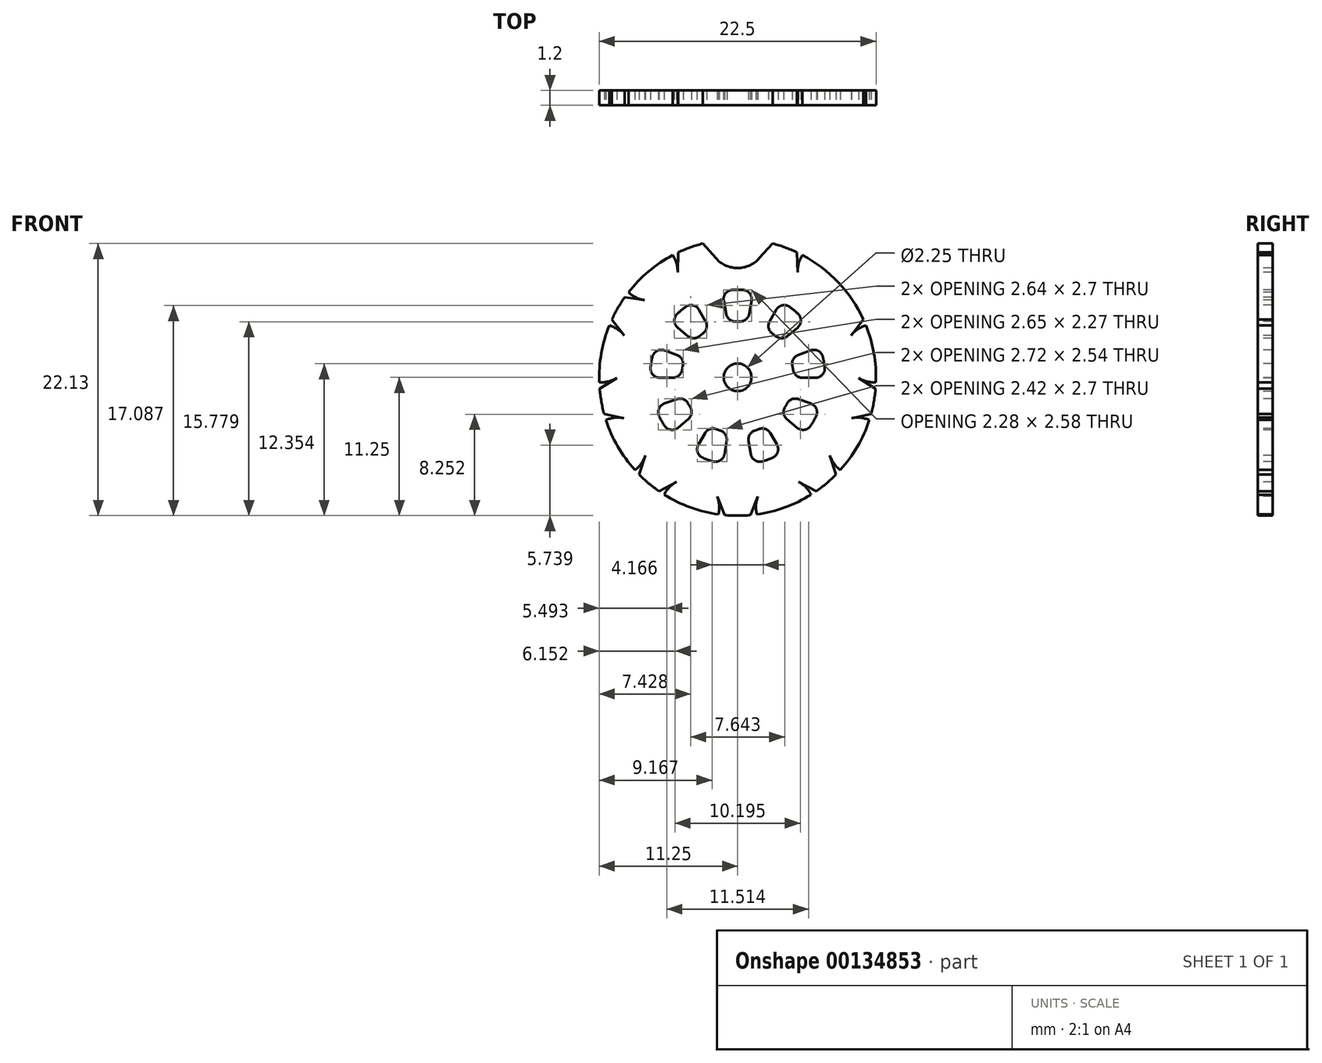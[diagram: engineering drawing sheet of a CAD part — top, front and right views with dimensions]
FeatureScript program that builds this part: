
annotation { "Feature Type Name" : "Feature", "Feature Type Description" : "" }
export const myFeature = defineFeature(function(context is Context, id is Id, definition is map)
    precondition{}
    {
        {
            var Q0;
            Q0=qCreatedBy(makeId("Front.planeOp"),FACE);
            var sketch = newSketch(context, id + "F0", { "sketchPlane" : qUnion([Q0])});
            skCircle(sketch, "E0", {"center": v(0, 0) * mm, "radius": 7.5 * mm});
            skSolve(sketch);
        }
        {
            var Q0;
            Q0=qSketchRegion(id+"F0",true);
            extrude(context, id + "F1", {"entities" : qUnion([Q0]), "depth" : 0.8 * mm});
        }
        {
            var Q0;
            Q0=makeQuery(id+"F1.opExtrude","CAP_FACE",FACE,{"disambiguationData":[OSD([sQuery(id+"F0.wireOp",EDGE,"E0")])],"isStart":false});
            var sketch = newSketch(context, id + "F2", { "sketchPlane" : qUnion([Q0])});
            skCircle(sketch, "E1", {"center": v(0, 7.5) * mm, "radius": 1.57 * mm});
            skCircle(sketch, "E2", {"center": v(4.82, 5.75) * mm, "radius": 1.57 * mm});
            skLineSegment(sketch, "E3", {"start": v(0, 0) * mm, "end": v(4.82, 5.75) * mm, "construction": true});
            skLineSegment(sketch, "E4", {"start": v(0, 7.5) * mm, "end": v(4.82, 5.75) * mm, "construction": true});
            skLineSegment(sketch, "E5", {"start": v(0, 0) * mm, "end": v(2.41, 6.62) * mm, "construction": true});
            skLineSegment(sketch, "E6", {"start": v(2.23, 7.63) * mm, "end": v(1.17, 6.45) * mm});
            skLineSegment(sketch, "E7.MirrorCS", {"start": v(3.2, 7.28) * mm, "end": v(3.25, 5.7) * mm});
            skLineSegment(sketch, "E8", {"start": v(2.23, 7.63) * mm, "end": v(3.2, 7.28) * mm});
            skCircle(sketch, "E9.1.0", {"center": v(-4.82, 5.75) * mm, "radius": 1.57 * mm});
            skLineSegment(sketch, "E9.1.1", {"start": v(-3.2, 7.28) * mm, "end": v(-3.25, 5.7) * mm});
            skLineSegment(sketch, "E9.1.2", {"start": v(-3.2, 7.28) * mm, "end": v(-2.23, 7.63) * mm});
            skLineSegment(sketch, "E9.1.3", {"start": v(-2.23, 7.63) * mm, "end": v(-1.17, 6.45) * mm});
            skCircle(sketch, "E9.2.0", {"center": v(-7.39, 1.3) * mm, "radius": 1.57 * mm});
            skLineSegment(sketch, "E9.2.1", {"start": v(-7.13, 3.52) * mm, "end": v(-6.15, 2.27) * mm});
            skLineSegment(sketch, "E9.2.2", {"start": v(-7.13, 3.52) * mm, "end": v(-6.61, 4.41) * mm});
            skLineSegment(sketch, "E9.2.3", {"start": v(-6.61, 4.41) * mm, "end": v(-5.04, 4.19) * mm});
            skCircle(sketch, "E9.2.4", {"center": v(-4.82, 5.75) * mm, "radius": 1.57 * mm});
            skCircle(sketch, "E9.3.0", {"center": v(-6.5, -3.75) * mm, "radius": 1.57 * mm});
            skLineSegment(sketch, "E9.3.1", {"start": v(-7.72, -1.88) * mm, "end": v(-6.17, -2.21) * mm});
            skLineSegment(sketch, "E9.3.2", {"start": v(-7.72, -1.88) * mm, "end": v(-7.9, -0.87) * mm});
            skLineSegment(sketch, "E9.3.3", {"start": v(-7.9, -0.87) * mm, "end": v(-6.55, -0.03) * mm});
            skCircle(sketch, "E9.3.4", {"center": v(-7.39, 1.3) * mm, "radius": 1.57 * mm});
            skCircle(sketch, "E9.4.0", {"center": v(-2.57, -7.05) * mm, "radius": 1.57 * mm});
            skLineSegment(sketch, "E9.4.1", {"start": v(-4.7, -6.4) * mm, "end": v(-3.3, -5.66) * mm});
            skLineSegment(sketch, "E9.4.2", {"start": v(-4.7, -6.4) * mm, "end": v(-5.5, -5.74) * mm});
            skLineSegment(sketch, "E9.4.3", {"start": v(-5.5, -5.74) * mm, "end": v(-5, -4.24) * mm});
            skCircle(sketch, "E9.4.4", {"center": v(-6.5, -3.75) * mm, "radius": 1.57 * mm});
            skCircle(sketch, "E9.5.0", {"center": v(2.57, -7.05) * mm, "radius": 1.57 * mm});
            skLineSegment(sketch, "E9.5.1", {"start": v(0.51, -7.93) * mm, "end": v(1.1, -6.46) * mm});
            skLineSegment(sketch, "E9.5.2", {"start": v(0.51, -7.93) * mm, "end": v(-0.51, -7.93) * mm});
            skLineSegment(sketch, "E9.5.3", {"start": v(-0.51, -7.93) * mm, "end": v(-1.1, -6.46) * mm});
            skCircle(sketch, "E9.5.4", {"center": v(-2.57, -7.05) * mm, "radius": 1.57 * mm});
            skCircle(sketch, "E9.6.0", {"center": v(6.5, -3.75) * mm, "radius": 1.57 * mm});
            skLineSegment(sketch, "E9.6.1", {"start": v(5.5, -5.74) * mm, "end": v(5, -4.24) * mm});
            skLineSegment(sketch, "E9.6.2", {"start": v(5.5, -5.74) * mm, "end": v(4.7, -6.4) * mm});
            skLineSegment(sketch, "E9.6.3", {"start": v(4.7, -6.4) * mm, "end": v(3.3, -5.66) * mm});
            skCircle(sketch, "E9.6.4", {"center": v(2.57, -7.05) * mm, "radius": 1.57 * mm});
            skCircle(sketch, "E9.7.0", {"center": v(7.39, 1.3) * mm, "radius": 1.57 * mm});
            skLineSegment(sketch, "E9.7.1", {"start": v(7.9, -0.87) * mm, "end": v(6.55, -0.03) * mm});
            skLineSegment(sketch, "E9.7.2", {"start": v(7.9, -0.87) * mm, "end": v(7.72, -1.88) * mm});
            skLineSegment(sketch, "E9.7.3", {"start": v(7.72, -1.88) * mm, "end": v(6.17, -2.21) * mm});
            skCircle(sketch, "E9.7.4", {"center": v(6.5, -3.75) * mm, "radius": 1.57 * mm});
            skLineSegment(sketch, "E9.8.1", {"start": v(6.61, 4.41) * mm, "end": v(5.04, 4.19) * mm});
            skLineSegment(sketch, "E9.8.2", {"start": v(6.61, 4.41) * mm, "end": v(7.13, 3.52) * mm});
            skLineSegment(sketch, "E9.8.3", {"start": v(7.13, 3.52) * mm, "end": v(6.15, 2.27) * mm});
            skCircle(sketch, "E9.8.4", {"center": v(7.39, 1.3) * mm, "radius": 1.57 * mm});
            skPoint(sketch, "E9.center", {"position": v(0, 0) * mm});
            skSolve(sketch);
        }
        {
            var Q0;
            {var subQ1=sQuery(id+"F2.wireOp",EDGE,"E1");var subQ5=makeQuery(id+"F2.imprint","INTERSECT",VERTEX,{"derivedFrom":[sQuery(id+"F2.wireOp",EDGE,"E9.1.3"),subQ1]});Q0=makeQuery(id+"F2.imprint","IMPRINT",FACE,{"disambiguationData":[TD([[makeQuery(id+"F2.imprint","IMPRINT",EDGE,{"disambiguationData":[TD([[subQ5,1.0]])],"derivedFrom":subQ1}),1.0]])]});}
            var Q1;
            {var subQ1=sQuery(id+"F2.wireOp",EDGE,"E1");var subQ3=sQuery(id+"F2.wireOp",EDGE,"E6");var subQ5=makeQuery(id+"F2.imprint","INTERSECT",VERTEX,{"derivedFrom":[subQ3,subQ1]});Q1=makeQuery(id+"F2.imprint","IMPRINT",FACE,{"disambiguationData":[TD([[makeQuery(id+"F2.imprint","IMPRINT",EDGE,{"disambiguationData":[TD([[subQ5,1.0]])],"derivedFrom":subQ3}),-1.0]])]});}
            var Q2;
            {var subQ1=sQuery(id+"F2.wireOp",EDGE,"E2");var subQ3=sQuery(id+"F2.wireOp",EDGE,"E7.MirrorCS");var subQ5=makeQuery(id+"F2.imprint","INTERSECT",VERTEX,{"derivedFrom":[subQ3,subQ1]});Q2=makeQuery(id+"F2.imprint","IMPRINT",FACE,{"disambiguationData":[TD([[makeQuery(id+"F2.imprint","IMPRINT",EDGE,{"disambiguationData":[TD([[subQ5,1.0]])],"derivedFrom":subQ3}),1.0]])]});}
            var Q3;
            {var subQ1=sQuery(id+"F2.wireOp",EDGE,"E2");var subQ5=makeQuery(id+"F2.imprint","INTERSECT",VERTEX,{"derivedFrom":[sQuery(id+"F2.wireOp",EDGE,"E7.MirrorCS"),subQ1]});Q3=makeQuery(id+"F2.imprint","IMPRINT",FACE,{"disambiguationData":[TD([[makeQuery(id+"F2.imprint","IMPRINT",EDGE,{"disambiguationData":[TD([[subQ5,1.0]])],"derivedFrom":subQ1}),1.0]])]});}
            var Q4;
            {var subQ1=sQuery(id+"F2.wireOp",EDGE,"E9.8.1");var subQ3=sQuery(id+"F2.wireOp",EDGE,"E2");var subQ5=makeQuery(id+"F2.imprint","INTERSECT",VERTEX,{"derivedFrom":[subQ3,subQ1]});Q4=makeQuery(id+"F2.imprint","IMPRINT",FACE,{"disambiguationData":[TD([[makeQuery(id+"F2.imprint","IMPRINT",EDGE,{"disambiguationData":[TD([[subQ5,-1.0]])],"derivedFrom":subQ3}),-1.0]])]});}
            var Q5;
            {var subQ1=sQuery(id+"F2.wireOp",EDGE,"E9.8.4");var subQ3=sQuery(id+"F2.wireOp",EDGE,"E9.8.3");var subQ5=makeQuery(id+"F2.imprint","INTERSECT",VERTEX,{"derivedFrom":[subQ3,subQ1]});Q5=makeQuery(id+"F2.imprint","IMPRINT",FACE,{"disambiguationData":[TD([[makeQuery(id+"F2.imprint","IMPRINT",EDGE,{"disambiguationData":[TD([[subQ5,1.0]])],"derivedFrom":subQ3}),1.0]])]});}
            var Q6;
            {var subQ1=sQuery(id+"F2.wireOp",EDGE,"E9.8.4");var subQ5=makeQuery(id+"F2.imprint","INTERSECT",VERTEX,{"derivedFrom":[sQuery(id+"F2.wireOp",EDGE,"E9.8.3"),subQ1]});Q6=makeQuery(id+"F2.imprint","IMPRINT",FACE,{"disambiguationData":[TD([[makeQuery(id+"F2.imprint","IMPRINT",EDGE,{"disambiguationData":[TD([[subQ5,1.0]])],"derivedFrom":subQ1}),1.0]])]});}
            var Q7;
            {var subQ1=sQuery(id+"F2.wireOp",EDGE,"E9.8.4");var subQ3=sQuery(id+"F2.wireOp",EDGE,"E9.7.1");var subQ5=makeQuery(id+"F2.imprint","INTERSECT",VERTEX,{"derivedFrom":[subQ3,subQ1]});Q7=makeQuery(id+"F2.imprint","IMPRINT",FACE,{"disambiguationData":[TD([[makeQuery(id+"F2.imprint","IMPRINT",EDGE,{"disambiguationData":[TD([[subQ5,1.0]])],"derivedFrom":subQ3}),-1.0]])]});}
            var Q8;
            {var subQ1=sQuery(id+"F2.wireOp",EDGE,"E9.7.4");var subQ3=sQuery(id+"F2.wireOp",EDGE,"E9.7.3");var subQ5=makeQuery(id+"F2.imprint","INTERSECT",VERTEX,{"derivedFrom":[subQ3,subQ1]});Q8=makeQuery(id+"F2.imprint","IMPRINT",FACE,{"disambiguationData":[TD([[makeQuery(id+"F2.imprint","IMPRINT",EDGE,{"disambiguationData":[TD([[subQ5,1.0]])],"derivedFrom":subQ3}),1.0]])]});}
            var Q9;
            {var subQ1=sQuery(id+"F2.wireOp",EDGE,"E9.7.4");var subQ5=makeQuery(id+"F2.imprint","INTERSECT",VERTEX,{"derivedFrom":[sQuery(id+"F2.wireOp",EDGE,"E9.7.3"),subQ1]});Q9=makeQuery(id+"F2.imprint","IMPRINT",FACE,{"disambiguationData":[TD([[makeQuery(id+"F2.imprint","IMPRINT",EDGE,{"disambiguationData":[TD([[subQ5,1.0]])],"derivedFrom":subQ1}),1.0]])]});}
            var Q10;
            {var subQ1=sQuery(id+"F2.wireOp",EDGE,"E9.7.4");var subQ3=sQuery(id+"F2.wireOp",EDGE,"E9.6.1");var subQ5=makeQuery(id+"F2.imprint","INTERSECT",VERTEX,{"derivedFrom":[subQ3,subQ1]});Q10=makeQuery(id+"F2.imprint","IMPRINT",FACE,{"disambiguationData":[TD([[makeQuery(id+"F2.imprint","IMPRINT",EDGE,{"disambiguationData":[TD([[subQ5,1.0]])],"derivedFrom":subQ3}),-1.0]])]});}
            var Q11;
            {var subQ1=sQuery(id+"F2.wireOp",EDGE,"E9.6.4");var subQ3=sQuery(id+"F2.wireOp",EDGE,"E9.6.3");var subQ5=makeQuery(id+"F2.imprint","INTERSECT",VERTEX,{"derivedFrom":[subQ3,subQ1]});Q11=makeQuery(id+"F2.imprint","IMPRINT",FACE,{"disambiguationData":[TD([[makeQuery(id+"F2.imprint","IMPRINT",EDGE,{"disambiguationData":[TD([[subQ5,1.0]])],"derivedFrom":subQ3}),1.0]])]});}
            var Q12;
            {var subQ1=sQuery(id+"F2.wireOp",EDGE,"E9.6.4");var subQ5=makeQuery(id+"F2.imprint","INTERSECT",VERTEX,{"derivedFrom":[sQuery(id+"F2.wireOp",EDGE,"E9.6.3"),subQ1]});Q12=makeQuery(id+"F2.imprint","IMPRINT",FACE,{"disambiguationData":[TD([[makeQuery(id+"F2.imprint","IMPRINT",EDGE,{"disambiguationData":[TD([[subQ5,1.0]])],"derivedFrom":subQ1}),1.0]])]});}
            var Q13;
            {var subQ1=sQuery(id+"F2.wireOp",EDGE,"E9.6.4");var subQ3=sQuery(id+"F2.wireOp",EDGE,"E9.5.1");var subQ5=makeQuery(id+"F2.imprint","INTERSECT",VERTEX,{"derivedFrom":[subQ3,subQ1]});Q13=makeQuery(id+"F2.imprint","IMPRINT",FACE,{"disambiguationData":[TD([[makeQuery(id+"F2.imprint","IMPRINT",EDGE,{"disambiguationData":[TD([[subQ5,1.0]])],"derivedFrom":subQ3}),-1.0]])]});}
            var Q14;
            {var subQ1=sQuery(id+"F2.wireOp",EDGE,"E9.5.4");var subQ3=sQuery(id+"F2.wireOp",EDGE,"E9.5.3");var subQ5=makeQuery(id+"F2.imprint","INTERSECT",VERTEX,{"derivedFrom":[subQ3,subQ1]});Q14=makeQuery(id+"F2.imprint","IMPRINT",FACE,{"disambiguationData":[TD([[makeQuery(id+"F2.imprint","IMPRINT",EDGE,{"disambiguationData":[TD([[subQ5,1.0]])],"derivedFrom":subQ3}),1.0]])]});}
            var Q15;
            {var subQ1=sQuery(id+"F2.wireOp",EDGE,"E9.5.4");var subQ5=makeQuery(id+"F2.imprint","INTERSECT",VERTEX,{"derivedFrom":[sQuery(id+"F2.wireOp",EDGE,"E9.5.3"),subQ1]});Q15=makeQuery(id+"F2.imprint","IMPRINT",FACE,{"disambiguationData":[TD([[makeQuery(id+"F2.imprint","IMPRINT",EDGE,{"disambiguationData":[TD([[subQ5,1.0]])],"derivedFrom":subQ1}),1.0]])]});}
            var Q16;
            {var subQ1=sQuery(id+"F2.wireOp",EDGE,"E9.5.4");var subQ3=sQuery(id+"F2.wireOp",EDGE,"E9.4.1");var subQ5=makeQuery(id+"F2.imprint","INTERSECT",VERTEX,{"derivedFrom":[subQ3,subQ1]});Q16=makeQuery(id+"F2.imprint","IMPRINT",FACE,{"disambiguationData":[TD([[makeQuery(id+"F2.imprint","IMPRINT",EDGE,{"disambiguationData":[TD([[subQ5,1.0]])],"derivedFrom":subQ3}),-1.0]])]});}
            var Q17;
            {var subQ1=sQuery(id+"F2.wireOp",EDGE,"E9.4.4");var subQ3=sQuery(id+"F2.wireOp",EDGE,"E9.4.3");var subQ5=makeQuery(id+"F2.imprint","INTERSECT",VERTEX,{"derivedFrom":[subQ3,subQ1]});Q17=makeQuery(id+"F2.imprint","IMPRINT",FACE,{"disambiguationData":[TD([[makeQuery(id+"F2.imprint","IMPRINT",EDGE,{"disambiguationData":[TD([[subQ5,1.0]])],"derivedFrom":subQ3}),1.0]])]});}
            var Q18;
            {var subQ1=sQuery(id+"F2.wireOp",EDGE,"E9.4.4");var subQ5=makeQuery(id+"F2.imprint","INTERSECT",VERTEX,{"derivedFrom":[sQuery(id+"F2.wireOp",EDGE,"E9.4.3"),subQ1]});Q18=makeQuery(id+"F2.imprint","IMPRINT",FACE,{"disambiguationData":[TD([[makeQuery(id+"F2.imprint","IMPRINT",EDGE,{"disambiguationData":[TD([[subQ5,1.0]])],"derivedFrom":subQ1}),1.0]])]});}
            var Q19;
            {var subQ1=sQuery(id+"F2.wireOp",EDGE,"E9.4.4");var subQ3=sQuery(id+"F2.wireOp",EDGE,"E9.3.1");var subQ5=makeQuery(id+"F2.imprint","INTERSECT",VERTEX,{"derivedFrom":[subQ3,subQ1]});Q19=makeQuery(id+"F2.imprint","IMPRINT",FACE,{"disambiguationData":[TD([[makeQuery(id+"F2.imprint","IMPRINT",EDGE,{"disambiguationData":[TD([[subQ5,1.0]])],"derivedFrom":subQ3}),-1.0]])]});}
            var Q20;
            {var subQ1=sQuery(id+"F2.wireOp",EDGE,"E9.3.4");var subQ3=sQuery(id+"F2.wireOp",EDGE,"E9.3.3");var subQ5=makeQuery(id+"F2.imprint","INTERSECT",VERTEX,{"derivedFrom":[subQ3,subQ1]});Q20=makeQuery(id+"F2.imprint","IMPRINT",FACE,{"disambiguationData":[TD([[makeQuery(id+"F2.imprint","IMPRINT",EDGE,{"disambiguationData":[TD([[subQ5,1.0]])],"derivedFrom":subQ3}),1.0]])]});}
            var Q21;
            {var subQ1=sQuery(id+"F2.wireOp",EDGE,"E9.3.4");var subQ5=makeQuery(id+"F2.imprint","INTERSECT",VERTEX,{"derivedFrom":[sQuery(id+"F2.wireOp",EDGE,"E9.3.3"),subQ1]});Q21=makeQuery(id+"F2.imprint","IMPRINT",FACE,{"disambiguationData":[TD([[makeQuery(id+"F2.imprint","IMPRINT",EDGE,{"disambiguationData":[TD([[subQ5,1.0]])],"derivedFrom":subQ1}),1.0]])]});}
            var Q22;
            {var subQ1=sQuery(id+"F2.wireOp",EDGE,"E9.3.4");var subQ3=sQuery(id+"F2.wireOp",EDGE,"E9.2.1");var subQ5=makeQuery(id+"F2.imprint","INTERSECT",VERTEX,{"derivedFrom":[subQ3,subQ1]});Q22=makeQuery(id+"F2.imprint","IMPRINT",FACE,{"disambiguationData":[TD([[makeQuery(id+"F2.imprint","IMPRINT",EDGE,{"disambiguationData":[TD([[subQ5,1.0]])],"derivedFrom":subQ3}),-1.0]])]});}
            var Q23;
            {var subQ1=sQuery(id+"F2.wireOp",EDGE,"E9.2.4");var subQ3=sQuery(id+"F2.wireOp",EDGE,"E9.2.3");var subQ5=makeQuery(id+"F2.imprint","INTERSECT",VERTEX,{"derivedFrom":[subQ3,subQ1]});Q23=makeQuery(id+"F2.imprint","IMPRINT",FACE,{"disambiguationData":[TD([[makeQuery(id+"F2.imprint","IMPRINT",EDGE,{"disambiguationData":[TD([[subQ5,1.0]])],"derivedFrom":subQ3}),1.0]])]});}
            var Q24;
            {var subQ1=sQuery(id+"F2.wireOp",EDGE,"E9.2.4");var subQ5=makeQuery(id+"F2.imprint","INTERSECT",VERTEX,{"derivedFrom":[sQuery(id+"F2.wireOp",EDGE,"E9.2.3"),subQ1]});Q24=makeQuery(id+"F2.imprint","IMPRINT",FACE,{"disambiguationData":[TD([[makeQuery(id+"F2.imprint","IMPRINT",EDGE,{"disambiguationData":[TD([[subQ5,1.0]])],"derivedFrom":subQ1}),1.0]])]});}
            var Q25;
            {var subQ1=sQuery(id+"F2.wireOp",EDGE,"E9.2.4");var subQ3=sQuery(id+"F2.wireOp",EDGE,"E9.1.1");var subQ5=makeQuery(id+"F2.imprint","INTERSECT",VERTEX,{"derivedFrom":[subQ3,subQ1]});Q25=makeQuery(id+"F2.imprint","IMPRINT",FACE,{"disambiguationData":[TD([[makeQuery(id+"F2.imprint","IMPRINT",EDGE,{"disambiguationData":[TD([[subQ5,1.0]])],"derivedFrom":subQ3}),-1.0]])]});}
            var Q26;
            {var subQ1=sQuery(id+"F2.wireOp",EDGE,"E1");var subQ3=sQuery(id+"F2.wireOp",EDGE,"E9.1.3");var subQ5=makeQuery(id+"F2.imprint","INTERSECT",VERTEX,{"derivedFrom":[subQ3,subQ1]});Q26=makeQuery(id+"F2.imprint","IMPRINT",FACE,{"disambiguationData":[TD([[makeQuery(id+"F2.imprint","IMPRINT",EDGE,{"disambiguationData":[TD([[subQ5,1.0]])],"derivedFrom":subQ3}),1.0]])]});}
            extrude(context, id + "F3", {"entities" : qUnion([Q0, Q1, Q2, Q3, Q4, Q5, Q6, Q7, Q8, Q9, Q10, Q11, Q12, Q13, Q14, Q15, Q16, Q17, Q18, Q19, Q20, Q21, Q22, Q23, Q24, Q25, Q26]), "operationType" : NewBodyOperationType.REMOVE, "endBound" : BoundingType.THROUGH_ALL, "oppositeDirection" : true, "depth" : 25 * mm});
        }
        {
            var Q0;
            Q0=makeQuery(id+"F1.opExtrude","CAP_FACE",FACE,{"disambiguationData":[OSD([sQuery(id+"F0.wireOp",EDGE,"E0")])],"isStart":false});
            var sketch = newSketch(context, id + "F4", { "sketchPlane" : qUnion([Q0])});
            skLineSegment(sketch, "E10.0.0", {"start": v(6.17, -2.21) * mm, "end": v(7.23, -1.99) * mm});
            skArc(sketch, "E10.0.1", {"start": v(7.23, -1.99) * mm, "mid": v(7.39, -1.3) * mm, "end": v(7.48, -0.6) * mm});
            skLineSegment(sketch, "E10.0.2", {"start": v(7.48, -0.6) * mm, "end": v(6.55, -0.03) * mm});
            skArc(sketch, "E10.0.3", {"start": v(6.55, -0.03) * mm, "mid": v(5.84, 1.03) * mm, "end": v(6.15, 2.27) * mm});
            skLineSegment(sketch, "E10.0.4", {"start": v(6.15, 2.27) * mm, "end": v(6.82, 3.13) * mm});
            skArc(sketch, "E10.0.5", {"start": v(6.82, 3.13) * mm, "mid": v(6.5, 3.75) * mm, "end": v(6.12, 4.34) * mm});
            skLineSegment(sketch, "E10.0.6", {"start": v(6.12, 4.34) * mm, "end": v(5.04, 4.19) * mm});
            skArc(sketch, "E10.0.7", {"start": v(5.04, 4.19) * mm, "mid": v(3.8, 4.54) * mm, "end": v(3.25, 5.7) * mm});
            skLineSegment(sketch, "E10.0.8", {"start": v(3.25, 5.7) * mm, "end": v(3.21, 6.78) * mm});
            skArc(sketch, "E10.0.9", {"start": v(3.21, 6.78) * mm, "mid": v(2.57, 7.05) * mm, "end": v(1.9, 7.26) * mm});
            skLineSegment(sketch, "E10.0.10", {"start": v(1.9, 7.26) * mm, "end": v(1.17, 6.45) * mm});
            skArc(sketch, "E10.0.11", {"start": v(1.17, 6.45) * mm, "mid": v(0, 5.93) * mm, "end": v(-1.17, 6.45) * mm});
            skLineSegment(sketch, "E10.0.12", {"start": v(-1.17, 6.45) * mm, "end": v(-1.9, 7.26) * mm});
            skArc(sketch, "E10.0.13", {"start": v(-1.9, 7.26) * mm, "mid": v(-2.57, 7.05) * mm, "end": v(-3.21, 6.78) * mm});
            skLineSegment(sketch, "E10.0.14", {"start": v(-3.21, 6.78) * mm, "end": v(-3.25, 5.7) * mm});
            skArc(sketch, "E10.0.15", {"start": v(-3.25, 5.7) * mm, "mid": v(-3.8, 4.54) * mm, "end": v(-5.04, 4.19) * mm});
            skLineSegment(sketch, "E10.0.16", {"start": v(-5.04, 4.19) * mm, "end": v(-6.12, 4.34) * mm});
            skArc(sketch, "E10.0.17", {"start": v(-6.12, 4.34) * mm, "mid": v(-6.5, 3.75) * mm, "end": v(-6.82, 3.13) * mm});
            skLineSegment(sketch, "E10.0.18", {"start": v(-6.82, 3.13) * mm, "end": v(-6.15, 2.27) * mm});
            skArc(sketch, "E10.0.19", {"start": v(-6.15, 2.27) * mm, "mid": v(-5.84, 1.03) * mm, "end": v(-6.55, -0.03) * mm});
            skLineSegment(sketch, "E10.0.20", {"start": v(-6.55, -0.03) * mm, "end": v(-7.48, -0.6) * mm});
            skArc(sketch, "E10.0.21", {"start": v(-7.48, -0.6) * mm, "mid": v(-7.39, -1.3) * mm, "end": v(-7.23, -1.99) * mm});
            skLineSegment(sketch, "E10.0.22", {"start": v(-7.23, -1.99) * mm, "end": v(-6.17, -2.21) * mm});
            skArc(sketch, "E10.0.23", {"start": v(-6.17, -2.21) * mm, "mid": v(-5.13, -2.96) * mm, "end": v(-5, -4.24) * mm});
            skLineSegment(sketch, "E10.0.24", {"start": v(-5, -4.24) * mm, "end": v(-5.34, -5.27) * mm});
            skArc(sketch, "E10.0.25", {"start": v(-5.34, -5.27) * mm, "mid": v(-4.82, -5.75) * mm, "end": v(-4.26, -6.17) * mm});
            skLineSegment(sketch, "E10.0.26", {"start": v(-4.26, -6.17) * mm, "end": v(-3.3, -5.66) * mm});
            skArc(sketch, "E10.0.27", {"start": v(-3.3, -5.66) * mm, "mid": v(-2.03, -5.57) * mm, "end": v(-1.1, -6.46) * mm});
            skLineSegment(sketch, "E10.0.28", {"start": v(-1.1, -6.46) * mm, "end": v(-0.7, -7.47) * mm});
            skArc(sketch, "E10.0.29", {"start": v(-0.7, -7.47) * mm, "mid": v(0, -7.5) * mm, "end": v(0.7, -7.47) * mm});
            skLineSegment(sketch, "E10.0.30", {"start": v(0.7, -7.47) * mm, "end": v(1.1, -6.46) * mm});
            skArc(sketch, "E10.0.31", {"start": v(1.1, -6.46) * mm, "mid": v(2.03, -5.57) * mm, "end": v(3.3, -5.66) * mm});
            skLineSegment(sketch, "E10.0.32", {"start": v(3.3, -5.66) * mm, "end": v(4.26, -6.17) * mm});
            skArc(sketch, "E10.0.33", {"start": v(4.26, -6.17) * mm, "mid": v(4.82, -5.75) * mm, "end": v(5.34, -5.27) * mm});
            skLineSegment(sketch, "E10.0.34", {"start": v(5.34, -5.27) * mm, "end": v(5, -4.24) * mm});
            skArc(sketch, "E10.0.35", {"start": v(5, -4.24) * mm, "mid": v(5.13, -2.96) * mm, "end": v(6.17, -2.21) * mm});
            skLineSegment(sketch, "E11", {"start": v(-1.17, 6.45) * mm, "end": v(0, 0) * mm});
            skLineSegment(sketch, "E12", {"start": v(1.17, 6.45) * mm, "end": v(0, 0) * mm});
            skCircle(sketch, "E13", {"center": v(0, 0) * mm, "radius": 3.03 * mm});
            skCircle(sketch, "E14", {"center": v(0, 0) * mm, "radius": 4.75 * mm});
            skSolve(sketch);
        }
        {
            var Q0;
            {var subQ0=sQuery(id+"F4.wireOp",EDGE,"E14");var subQ3=sQuery(id+"F4.wireOp",EDGE,"E11");var subQ4=makeQuery(id+"F4.imprint","INTERSECT",VERTEX,{"derivedFrom":[subQ3,subQ0]});Q0=makeQuery(id+"F4.imprint","IMPRINT",FACE,{"disambiguationData":[TD([[makeQuery(id+"F4.imprint","IMPRINT",EDGE,{"disambiguationData":[TD([[subQ4,-1.0]])],"derivedFrom":subQ3}),1.0]])]});}
            var Q1;
            Q1=makeQuery(id+"F1.opExtrude","CAP_FACE",FACE,{"disambiguationData":[OSD([sQuery(id+"F0.wireOp",EDGE,"E0")])],"isStart":true});
            extrude(context, id + "F5", {"entities" : qUnion([Q0]), "endBound" : BoundingType.UP_TO_SURFACE, "oppositeDirection" : true, "endBoundEntityFace" : qUnion([Q1]), "depth" : 25 * mm});
        }
        {
            var Q0;
            Q0=makeQuery(id+"F5.opExtrude","SWEPT_EDGE",EDGE,{"disambiguationData":[OSD([sQuery(id+"F4.wireOp",EDGE,"E11"),sQuery(id+"F4.wireOp",EDGE,"E14")])]});
            var Q1;
            Q1=makeQuery(id+"F5.opExtrude","SWEPT_EDGE",EDGE,{"disambiguationData":[OSD([sQuery(id+"F4.wireOp",EDGE,"E11"),sQuery(id+"F4.wireOp",EDGE,"E13")])]});
            var Q2;
            Q2=makeQuery(id+"F5.opExtrude","SWEPT_EDGE",EDGE,{"disambiguationData":[OSD([sQuery(id+"F4.wireOp",EDGE,"E12"),sQuery(id+"F4.wireOp",EDGE,"E13")])]});
            var Q3;
            Q3=makeQuery(id+"F5.opExtrude","SWEPT_EDGE",EDGE,{"disambiguationData":[OSD([sQuery(id+"F4.wireOp",EDGE,"E12"),sQuery(id+"F4.wireOp",EDGE,"E14")])]});
            fillet(context, id + "F6", {"entities" : qUnion([Q0, Q1, Q2, Q3]), "radius" : 0.5 * mm, "allowEdgeOverflow" : false});
        }
        {
            var Q0;
            Q0=makeQuery(id+"F5.opExtrude","SWEPT_BODY",BODY,{"disambiguationData":[OSD([sQuery(id+"F4.wireOp",EDGE,"E11"),sQuery(id+"F4.wireOp",EDGE,"E12"),sQuery(id+"F4.wireOp",EDGE,"E13"),sQuery(id+"F4.wireOp",EDGE,"E14")])]});
            var Q1;
            Q1=makeQuery(id+"F5.opExtrude","CAP_EDGE",EDGE,{"disambiguationData":[OSD([sQuery(id+"F4.wireOp",EDGE,"E13")])],"isStart":true});
            circularPattern(context, id + "F7", {"operationType" : NewBodyOperationType.REMOVE, "entities" : qUnion([Q0]), "axis" : qUnion([Q1]), "angle" : 40 * degree, "instanceCount" : 9});
        }
        {
            var Q0;
            Q0=makeQuery(id+"F1.opExtrude","CAP_FACE",FACE,{"disambiguationData":[OSD([sQuery(id+"F0.wireOp",EDGE,"E0")])],"isStart":false});
            var sketch = newSketch(context, id + "F8", { "sketchPlane" : qUnion([Q0])});
            skCircle(sketch, "E15", {"center": v(0, 0) * mm, "radius": 0.75 * mm});
            skSolve(sketch);
        }
        {
            var Q0;
            Q0=makeQuery(id+"F8.imprint","IMPRINT",FACE,{"disambiguationData":[TD([[makeQuery(id+"F8.imprint","IMPRINT",EDGE,{"derivedFrom":sQuery(id+"F8.wireOp",EDGE,"E15")}),1.0]])]});
            extrude(context, id + "F9", {"entities" : qUnion([Q0]), "operationType" : NewBodyOperationType.REMOVE, "endBound" : BoundingType.THROUGH_ALL, "oppositeDirection" : true, "depth" : 25 * mm});
        }
        {
            var Q0;
            Q0=makeQuery(id+"F1.opExtrude","SWEPT_BODY",BODY,{"disambiguationData":[OSD([sQuery(id+"F0.wireOp",EDGE,"E0")])]});
            var Q1;
            Q1=sQuery(id+"F8.wireOp",VERTEX,"E15.center");
            transform(context, id + "F10", {"entities" : qUnion([Q0]), "transformType" : TransformType.SCALE_UNIFORMLY, "scale" : 1.5, "makeCopy" : false, "scalePoint" : qUnion([Q1])});
        }
        {
            var Q0;
            Q0=makeQuery(id+"F1.opExtrude","SWEPT_BODY",BODY,{"disambiguationData":[OSD([sQuery(id+"F0.wireOp",EDGE,"E0")])]});
            transform(context, id + "F11", {"entities" : qUnion([Q0]), "transformType" : TransformType.TRANSLATION_3D, "dx" : 25 * mm, "dy" : 0 * mm, "dz" : 0 * mm, "makeCopy" : true});
        }
        {
            var Q0;
            Q0=makeQuery(id+"F11.opPattern","COPY",BODY,{"derivedFrom":makeQuery(id+"F1.opExtrude","SWEPT_BODY",BODY,{"disambiguationData":[OSD([sQuery(id+"F0.wireOp",EDGE,"E0")])]}),"instanceName":"1"});
            var Q1;
            Q1=makeQuery(id+"F11.opPattern","COPY",VERTEX,{"derivedFrom":makeQuery(id+"F3.boolean.opBoolean","COPY",VERTEX,{"derivedFrom":makeQuery(id+"F3.opExtrude","CAP_VERTEX",VERTEX,{"disambiguationData":[OSD([sQuery(id+"F0.wireOp",EDGE,"E0"),sQuery(id+"F2.wireOp",EDGE,"E9.7.1")])],"isStart":true})}),"instanceName":"1"});
            transform(context, id + "F12", {"entities" : qUnion([Q0]), "transformType" : TransformType.SCALE_UNIFORMLY, "scale" : 0.67, "makeCopy" : false, "scalePoint" : qUnion([Q1])});
        }
        {
            var Q0;
            Q0=makeQuery(id+"F11.opPattern","COPY",BODY,{"derivedFrom":makeQuery(id+"F1.opExtrude","SWEPT_BODY",BODY,{"disambiguationData":[OSD([sQuery(id+"F0.wireOp",EDGE,"E0")])]}),"instanceName":"1"});
            deleteBodies(context, id + "F13", {"entities" : qUnion([Q0])});
        }
    });
